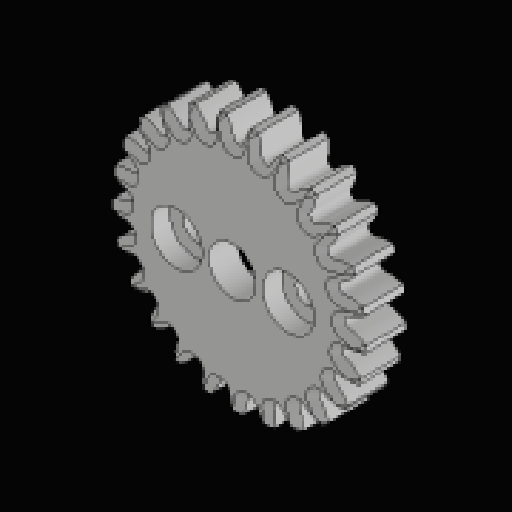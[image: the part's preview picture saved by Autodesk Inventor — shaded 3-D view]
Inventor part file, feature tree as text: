
AUTODESK INVENTOR PART (.ipt)
format: ipt  version: 2023.2 (Build 272271030, 271C)  size: 816,640 bytes
history: native  units: mm
features: sketch x4, extrude x3, chamfer x2, hole x2, pattern_circular x1
ambient origin geometry x8: Origin, YZ Plane, XZ Plane, XY Plane, X Axis, Y Axis, Z Axis, Center Point
bodies: Solid1 (feature_tree)
feature tree (12):
  sketch  "Sketch1"  dims[d0=5.0mm d1=0.0mm]
  extrude  "Extrusion1"  TaperAngle=0.0deg  [1 undecoded]
  extrude  "Extrusion2"  Depth=2.0mm TaperAngle=45.0deg
  chamfer  "Chamfer1"  Distance=2.0mm Angle=45.0deg
  chamfer  "Chamfer2"  Distance=250.0mm Angle=360.0deg
  pattern_circular  "Circular Pattern1"  [2 undecoded]
  extrude  "Extrusion3"  Depth=8.0mm
  sketch  "Sketch2"  dims[d2=0.0mm d3=0.0mm d4=0.7mm d5=2.0mm d6=45.0deg d7=0.7mm d8=2.0mm d9=45.0deg d10=250.0mm d11=360.0deg]
  sketch  "Sketch3"  dims[d13=6.0mm]
  sketch  "Sketch4"  dims[d14=11.9mm d15=20.594885mm d16=90.0deg d17=2.0mm d18=5.5mm d19=8.0mm d20=2.5mm d21=6.0mm d22=20.594885mm d23=90.0deg d24=2.0mm d25=6.0mm d26=8.0mm d27=5.0mm d28=8.0mm d29=10.0mm d30=2.0mm d31=0.0mm]
  hole  "Hole1"  [1 undecoded]
  hole  "Hole2"  [1 undecoded]
note: 5 required parameter values undecoded (feature->parameter linkage not recoverable at this tier; creation-order binding heuristic only, values carry confidence <= 0.55)
